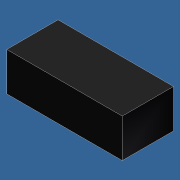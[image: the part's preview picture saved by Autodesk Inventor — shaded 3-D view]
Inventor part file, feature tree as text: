
AUTODESK INVENTOR PART (.ipt)
format: ipt  version: unknown  size: 166,400 bytes
history: native  units: mm
features: extrude x1, sketch x1
ambient origin geometry x8: Origin, YZ Plane, XZ Plane, XY Plane, X Axis, Y Axis, Z Axis, Center Point
feature tree (2):
  extrude  "Выдавливание2"  Depth=4.5mm
  sketch  "Эскиз2"
